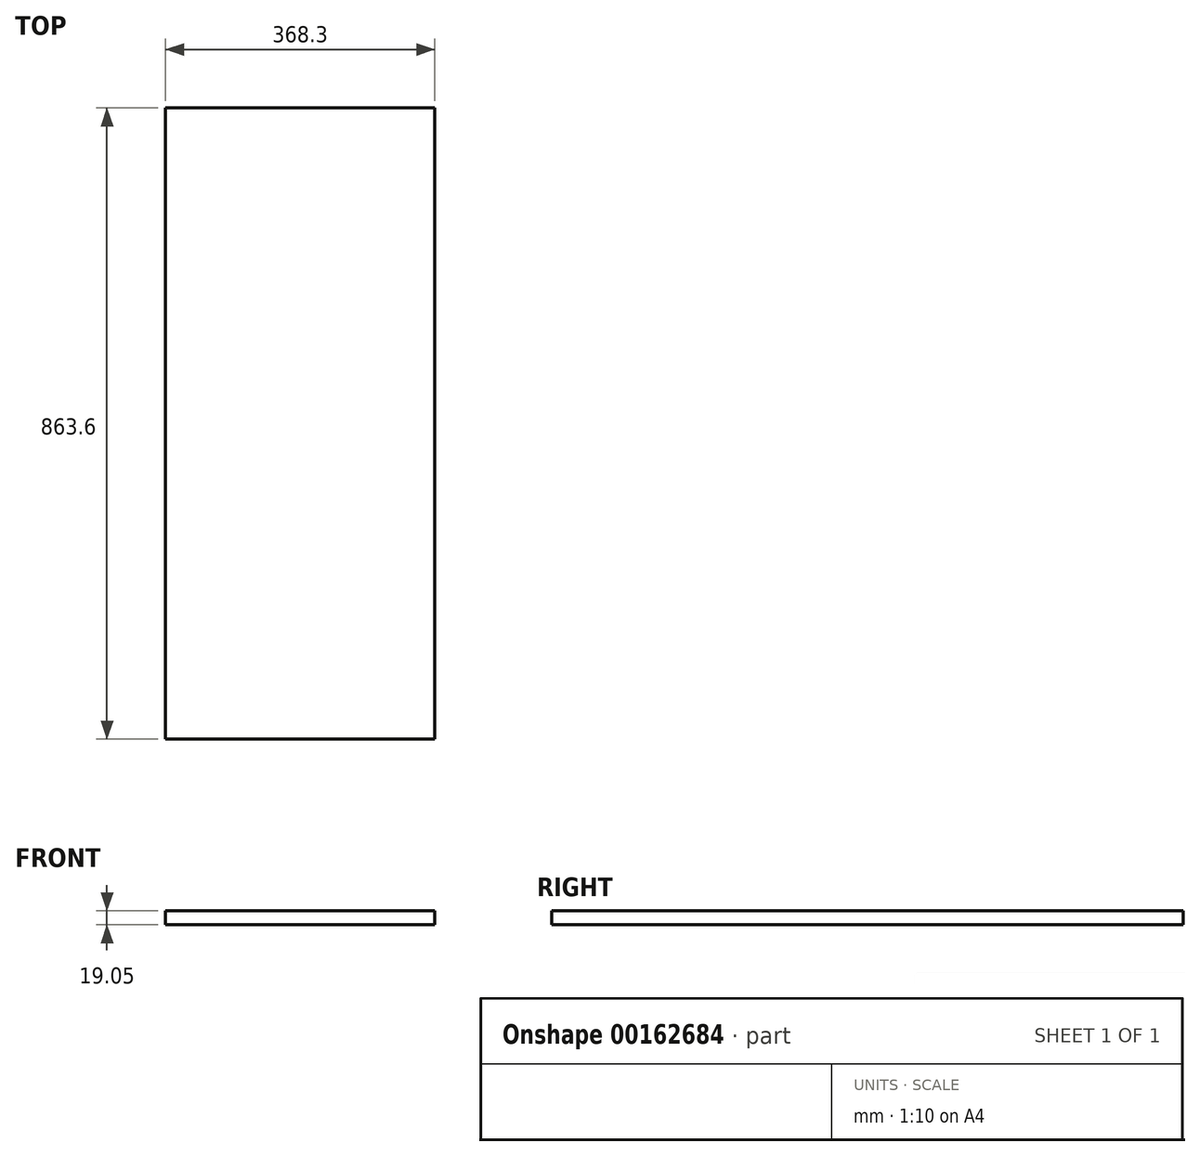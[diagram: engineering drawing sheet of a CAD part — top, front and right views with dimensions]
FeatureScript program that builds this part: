
annotation { "Feature Type Name" : "Feature", "Feature Type Description" : "" }
export const myFeature = defineFeature(function(context is Context, id is Id, definition is map)
    precondition{}
    {
        {
            var Q0;
            Q0=qCreatedBy(makeId("Top.planeOp"),FACE);
            var sketch = newSketch(context, id + "F0", { "sketchPlane" : qUnion([Q0])});
            skLineSegment(sketch, "E0.bottom", {"start": v(-183.43, 519.43) * mm, "end": v(184.87, 519.43) * mm});
            skLineSegment(sketch, "E0.top", {"start": v(-183.43, -344.17) * mm, "end": v(184.87, -344.17) * mm});
            skLineSegment(sketch, "E0.left", {"start": v(-183.43, 519.43) * mm, "end": v(-183.43, -344.17) * mm});
            skLineSegment(sketch, "E0.right", {"start": v(184.87, 519.43) * mm, "end": v(184.87, -344.17) * mm});
            skSolve(sketch);
        }
        {
            var Q0;
            Q0 = qSketchRegion(id + "F0", true);
            extrude(context, id + "F1", {"entities" : qUnion([Q0]), "depth" : 19.05 * mm});
        }
    });
